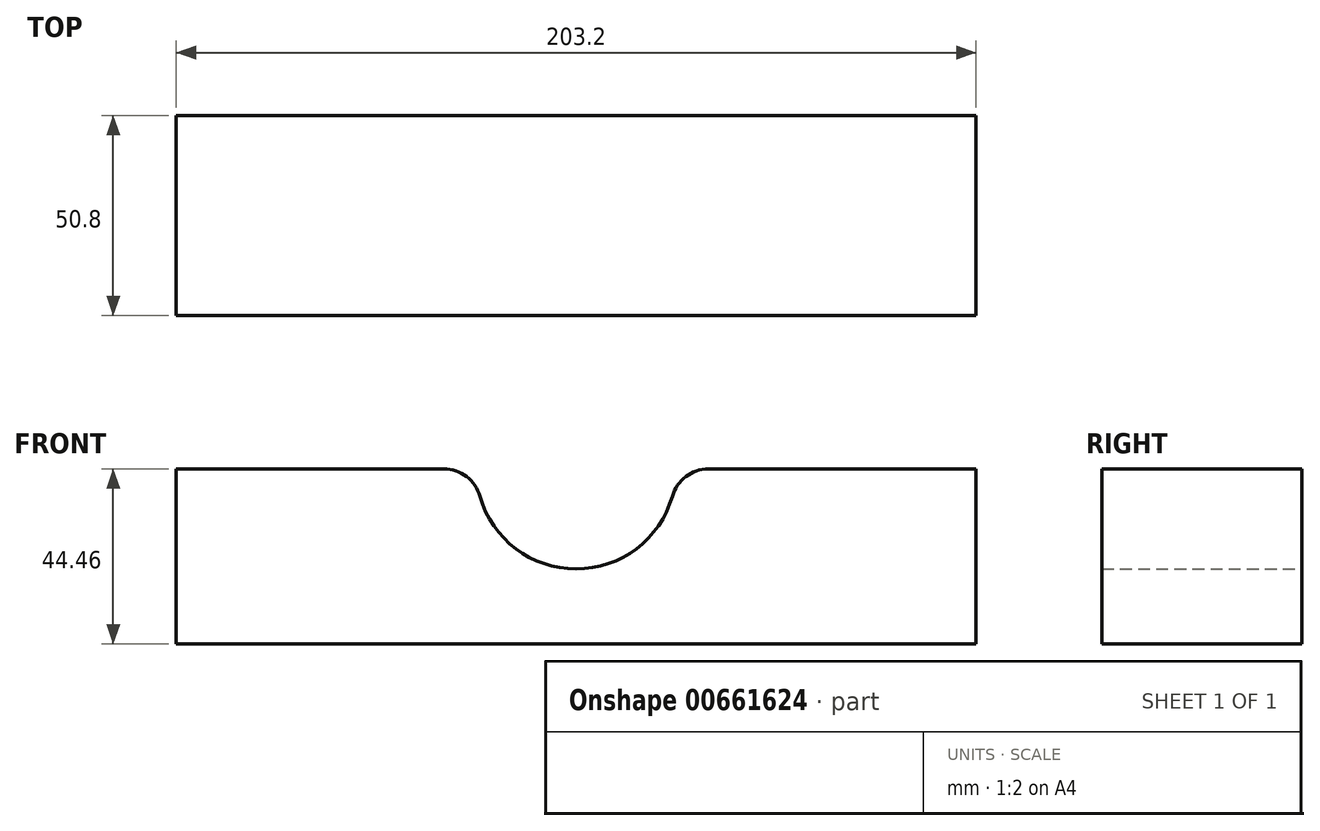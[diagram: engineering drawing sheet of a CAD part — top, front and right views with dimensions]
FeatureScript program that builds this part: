
annotation { "Feature Type Name" : "Feature", "Feature Type Description" : "" }
export const myFeature = defineFeature(function(context is Context, id is Id, definition is map)
    precondition{}
    {
        {
            var Q0;
            Q0=qCreatedBy(makeId("Front.planeOp"),FACE);
            var sketch = newSketch(context, id + "F0", { "sketchPlane" : qUnion([Q0])});
            skLineSegment(sketch, "E0.bottom", {"start": v(101.6, 22.23) * mm, "end": v(33.6, 22.23) * mm});
            skLineSegment(sketch, "E0.top", {"start": v(101.6, -22.22) * mm, "end": v(-101.6, -22.22) * mm});
            skLineSegment(sketch, "E0.left", {"start": v(101.6, 22.23) * mm, "end": v(101.6, -22.22) * mm});
            skLineSegment(sketch, "E0.right", {"start": v(-101.6, 22.23) * mm, "end": v(-101.6, -22.22) * mm});
            skPoint(sketch, "E0.middle", {"position": v(0, 0) * mm});
            skArc(sketch, "E1", {"start": v(-24.44, 15.3) * mm, "mid": v(0, -3.17) * mm, "end": v(24.44, 15.3) * mm});
            skLineSegment(sketch, "E2.trimOffspring", {"start": v(-33.6, 22.23) * mm, "end": v(-101.6, 22.23) * mm});
            skPoint(sketch, "E3.visualSharp", {"position": v(-25.4, 22.23) * mm});
            skArc(sketch, "E3.filletArc", {"start": v(-24.44, 15.3) * mm, "mid": v(-27.86, 20.3) * mm, "end": v(-33.6, 22.23) * mm});
            skPoint(sketch, "E4.visualSharp", {"position": v(25.4, 22.23) * mm});
            skArc(sketch, "E4.filletArc", {"start": v(33.6, 22.23) * mm, "mid": v(27.86, 20.3) * mm, "end": v(24.44, 15.3) * mm});
            skSolve(sketch);
        }
        {
            var Q0;
            Q0=makeQuery(id+"F0.imprint","IMPRINT",FACE,{"disambiguationData":[TD([[makeQuery(id+"F0.imprint","IMPRINT",EDGE,{"derivedFrom":sQuery(id+"F0.wireOp",EDGE,"E0.bottom")}),1.0]])]});
            extrude(context, id + "F1", {"entities" : qUnion([Q0]), "depth" : 50.8 * mm, "offsetDistance" : 25.4 * mm});
        }
    });
